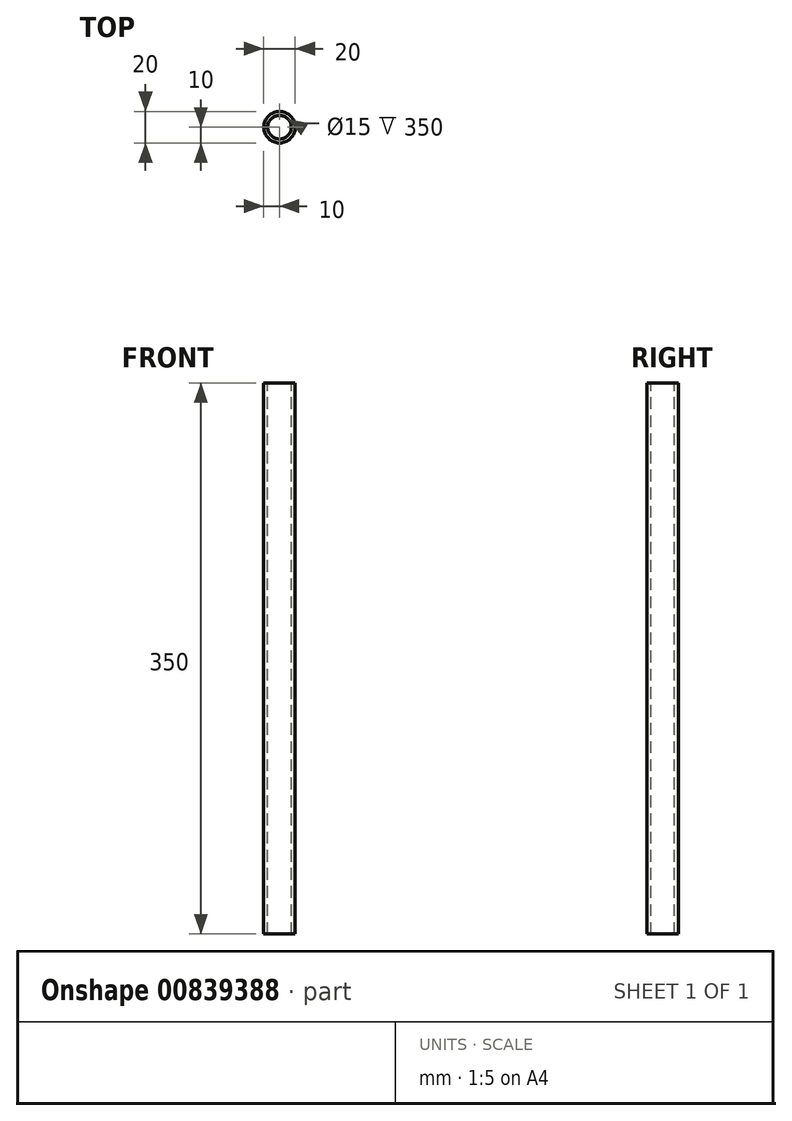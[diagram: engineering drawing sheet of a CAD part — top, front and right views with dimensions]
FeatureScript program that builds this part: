
annotation { "Feature Type Name" : "Feature", "Feature Type Description" : "" }
export const myFeature = defineFeature(function(context is Context, id is Id, definition is map)
    precondition{}
    {
        {
            var Q0;
            Q0=qCreatedBy(makeId("Top.planeOp"),FACE);
            var sketch = newSketch(context, id + "F0", { "sketchPlane" : qUnion([Q0])});
            skCircle(sketch, "E0", {"center": v(0, 0) * mm, "radius": 10 * mm});
            skSolve(sketch);
        }
        {
            var Q0;
            Q0=makeQuery(id+"F0.imprint","IMPRINT",FACE,{"disambiguationData":[TD([[makeQuery(id+"F0.imprint","IMPRINT",EDGE,{"derivedFrom":sQuery(id+"F0.wireOp",EDGE,"E0")}),1.0]])]});
            extrude(context, id + "F1", {"entities" : qUnion([Q0]), "endBound" : BoundingType.SYMMETRIC, "oppositeDirection" : true, "depth" : 350 * mm, "offsetDistance" : 25.4 * mm});
        }
        {
            var Q0;
            Q0=makeQuery(id+"F1.opExtrude","CAP_FACE",FACE,{"disambiguationData":[OSD([sQuery(id+"F0.wireOp",EDGE,"E0")])],"isStart":true});
            var Q1;
            Q1=makeQuery(id+"F1.opExtrude","CAP_FACE",FACE,{"disambiguationData":[OSD([sQuery(id+"F0.wireOp",EDGE,"E0")])],"isStart":false});
            shell(context, id + "F2", {"entities" : qUnion([Q0, Q1]), "thickness" : 2.5 * mm});
        }
    });
